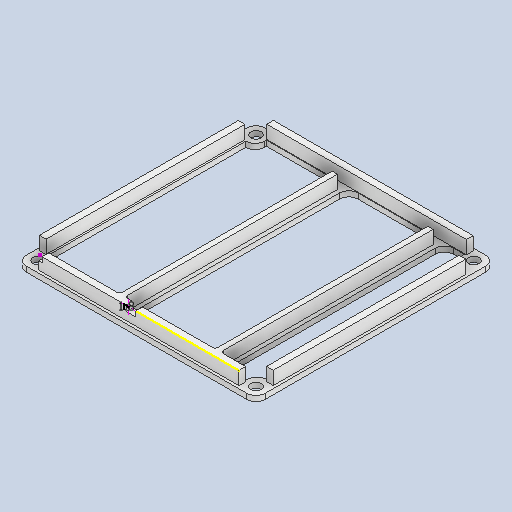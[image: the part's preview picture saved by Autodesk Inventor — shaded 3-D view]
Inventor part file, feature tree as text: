
AUTODESK INVENTOR PART (.ipt)
format: ipt  version: 2024 (Build 280153000, 153)  size: 348,160 bytes
history: native  units: mm
features: sketch x11, extrude x8, fillet x6, hole x1
ambient origin geometry x8: Origin, YZ Plane, XZ Plane, XY Plane, X Axis, Y Axis, Z Axis, Center Point
bodies: Solid1 (feature_tree)
feature tree (26):
  extrude  "Extrusion1"  Depth=90.0mm
  hole  "Hole1"  [1 undecoded]
  extrude  "Extrusion2"  Depth=2.0mm TaperAngle=0.0deg
  fillet  "Fillet1"  Radius=3.5mm
  sketch  "Sketch5"  dims[d21=4.0mm d22=2.0mm d23=0.0mm d24=3.5mm]
  extrude  "Extrusion4"  Depth=80.0mm
  extrude  "Extrusion5"  Depth=82.5mm
  fillet  "Fillet3"  Radius=32.5mm
  fillet  "Fillet4"  Radius=7.468mm
  fillet  "Fillet7"  Radius=82.5mm
  extrude  "Extrusion6"  Depth=3.5mm
  fillet  "Fillet8"  Radius=3.5mm
  fillet  "Fillet11"  Radius=4.5mm
  extrude  "Extrusion7"  Depth=4.0mm
  extrude  "Extrusion8"  Depth=2.0mm TaperAngle=0.0deg
  extrude  "Extrusion9"  Depth=1.0mm
  sketch  "Sketch23"  dims[d46=1.0mm d47=1.0mm]
  sketch  "Sketch24"  dims[d48=1.0mm d49=1.0mm d50=1.0mm d51=1.0mm d54=1.0mm d55=1.0mm d56=1.0mm d57=1.0mm d60=1.0mm d61=1.0mm d63=2.5mm d64=2.5mm d65=2.5mm d68=5.0mm d69=0.0mm d71=3.5mm d72=2.0mm d73=2.0mm d74=3.5mm d77=1.0mm d78=3.5mm d79=5.0mm d80=0.0mm d81=3.5mm d85=3.5mm d90=2.0mm d91=3.0mm d92=0.0mm d96=3.0mm d97=0.0mm d98=3.0mm d99=10.0mm d100=0.0mm d101=1.8mm d102=1.8mm d103=1.0mm d104=1.8mm d105=2.0mm d106=1.210778mm]
  sketch  "Sketch1"  dims[d2=90.0mm d3=90.0mm]
  sketch  "Sketch2"  dims[d4=2.0mm d5=0.0mm]
  sketch  "Sketch3"  dims[d8=4.0mm d9=6.0mm d10=4.0mm d11=2.0mm d12=90.0deg d13=8.0mm d14=20.594885mm d17=4.0mm]
  sketch  "Sketch8"  dims[d25=80.0mm d26=80.0mm]
  sketch  "Sketch10"  dims[d27=27.5mm d28=82.5mm d29=32.5mm d30=82.5mm d31=7.468mm d32=82.5mm]
  sketch  "Sketch19"  dims[d33=4.0mm d34=3.5mm d35=3.5mm d36=4.5mm]
  sketch  "Sketch21"  dims[d37=4.0mm d38=4.0mm]
  sketch  "Sketch22"  dims[d39=73.85mm d42=2.0mm d43=0.0mm]
note: 1 required parameter value undecoded (feature->parameter linkage not recoverable at this tier; creation-order binding heuristic only, values carry confidence <= 0.55)
